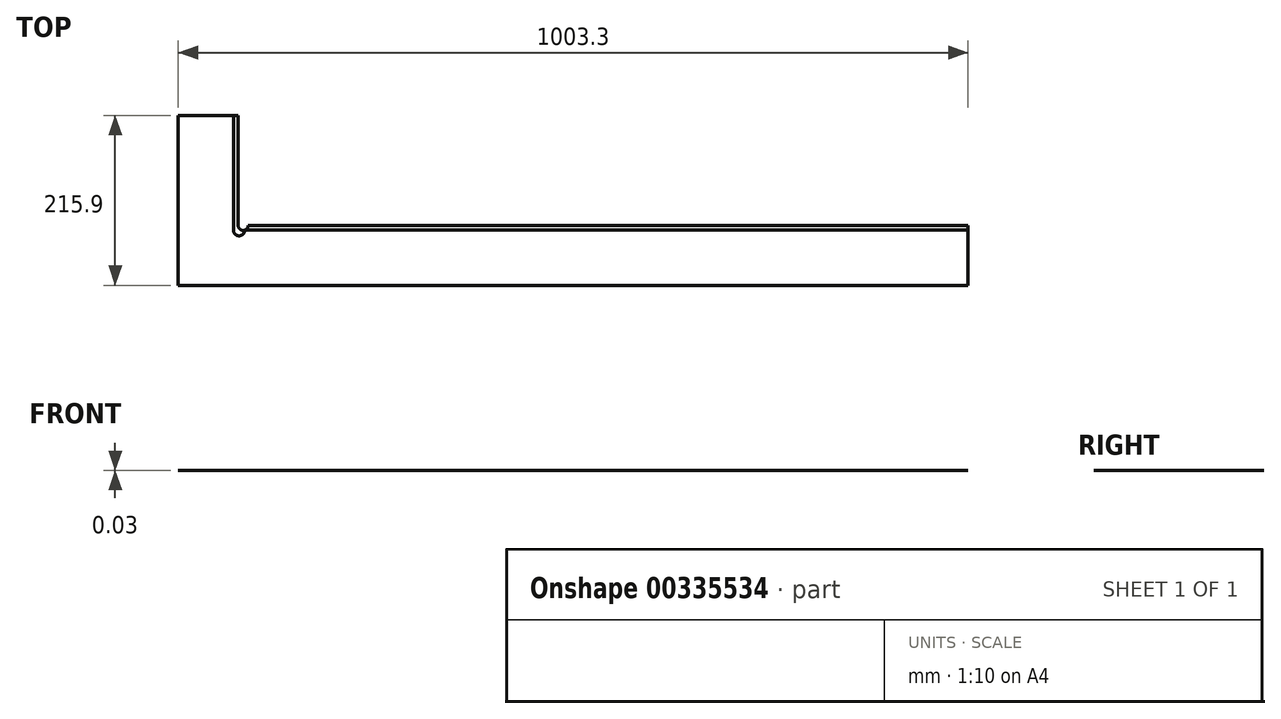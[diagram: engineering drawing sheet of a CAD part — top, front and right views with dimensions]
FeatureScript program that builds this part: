
annotation { "Feature Type Name" : "Feature", "Feature Type Description" : "" }
export const myFeature = defineFeature(function(context is Context, id is Id, definition is map)
    precondition{}
    {
        {
            var Q0;
            Q0=qCreatedBy(makeId("Top.planeOp"),FACE);
            var sketch = newSketch(context, id + "F0", { "sketchPlane" : qUnion([Q0])});
            skPoint(sketch, "E0.0", {"position": v(0, 0) * mm});
            skPoint(sketch, "E1.0", {"position": v(-6.1, -6.1) * mm});
            skPoint(sketch, "E2.0", {"position": v(0, 139.7) * mm});
            skLineSegment(sketch, "E3", {"start": v(12.7, 0) * mm, "end": v(927.1, 0) * mm});
            skLineSegment(sketch, "E4", {"start": v(927.1, 0) * mm, "end": v(927.1, -76.2) * mm});
            skLineSegment(sketch, "E5", {"start": v(927.1, -76.2) * mm, "end": v(-76.2, -76.2) * mm});
            skLineSegment(sketch, "E6", {"start": v(-76.2, -76.2) * mm, "end": v(-76.2, 139.7) * mm});
            skLineSegment(sketch, "E7", {"start": v(-76.2, 139.7) * mm, "end": v(0, 139.7) * mm});
            skLineSegment(sketch, "E8", {"start": v(0, 139.7) * mm, "end": v(0, 0) * mm});
            skLineSegment(sketch, "E9", {"start": v(-6.1, -6.1) * mm, "end": v(-6.1, 139.7) * mm});
            skArc(sketch, "E10", {"start": v(0, 0) * mm, "mid": v(6.35, -6.35) * mm, "end": v(12.7, 0) * mm});
            skArc(sketch, "E11", {"start": v(-6.1, -6.1) * mm, "mid": v(1.02, -13.2) * mm, "end": v(8.13, -6.1) * mm});
            skLineSegment(sketch, "E12.trimOffspring", {"start": v(8.13, -6.1) * mm, "end": v(927.1, -6.1) * mm});
            skSolve(sketch);
        }
        {
            var Q0;
            {var subQ4=sQuery(id+"F0.wireOp",EDGE,"E3");Q0=makeQuery(id+"F0.imprint","IMPRINT",FACE,{"disambiguationData":[TD([[makeQuery(id+"F0.imprint","IMPRINT",EDGE,{"derivedFrom":subQ4}),-1.0]])]});}
            var Q1;
            {var subQ3=sQuery(id+"F0.wireOp",EDGE,"E5");Q1=makeQuery(id+"F0.imprint","IMPRINT",FACE,{"disambiguationData":[TD([[makeQuery(id+"F0.imprint","IMPRINT",EDGE,{"derivedFrom":subQ3}),-1.0]])]});}
            var Q2;
            {var subQ1=sQuery(id+"F0.wireOp",EDGE,"E8");Q2=makeQuery(id+"F0.imprint","IMPRINT",FACE,{"disambiguationData":[TD([[makeQuery(id+"F0.imprint","IMPRINT",EDGE,{"derivedFrom":subQ1}),-1.0]])]});}
            extrude(context, id + "F1", {"entities" : qUnion([Q0, Q1, Q2]), "oppositeDirection" : true, "depth" : 5 / 203.2 * mm, "offsetDistance" : 25.4 * mm});
        }
        {
            var Q0;
            {var subQ3=sQuery(id+"F0.wireOp",EDGE,"E5");Q0=makeQuery(id+"F0.imprint","IMPRINT",FACE,{"disambiguationData":[TD([[makeQuery(id+"F0.imprint","IMPRINT",EDGE,{"derivedFrom":subQ3}),-1.0]])]});}
            extrude(context, id + "F2", {"entities" : qUnion([Q0]), "operationType" : NewBodyOperationType.ADD, "depth" : 1 / 101.6 * mm});
        }
    });
